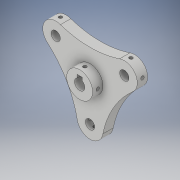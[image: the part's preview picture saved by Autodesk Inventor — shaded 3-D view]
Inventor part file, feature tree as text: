
AUTODESK INVENTOR PART (.ipt)
format: ipt  version: 2019 (Build 230136000, 136)  size: 257,536 bytes
history: native  units: mm
features: plane x10, sketch x9, hole x6, extrude x4, mirror x2, projected_geometry x2, other x1
ambient origin geometry x8: Origin, YZ Plane, XZ Plane, XY Plane, X Axis, Y Axis, Z Axis, Center Point
bodies: Body1 (feature_tree)
feature tree (34):
  other  "實體1"
  extrude  "擠出1"  Depth=109.5mm
  extrude  "擠出2"  Depth=43.5mm
  extrude  "擠出3"  Depth=76.5mm
  extrude  "擠出4"  Depth=25.0mm
  plane  "工作平面1"
  plane  "工作平面2"
  sketch  "草圖5"
  sketch  "草圖6"
  hole  "孔1"  [1 undecoded]
  hole  "孔2"  [1 undecoded]
  plane  "工作平面4"
  plane  "工作平面9"
  plane  "工作平面11"
  plane  "工作平面12"
  sketch  "草圖10"
  sketch  "草圖11"
  hole  "孔3"  [1 undecoded]
  hole  "孔4"  [1 undecoded]
  mirror  "鏡射1"
  hole  "孔5"  [1 undecoded]
  mirror  "鏡射2"
  plane  "工作平面14"
  plane  "工作平面15"
  hole  "孔7"  [1 undecoded]
  sketch  "草圖1"
  projected_geometry  "投影迴路1"
  sketch  "草圖3"
  sketch  "草圖4"
  projected_geometry  "投影迴路2"
  plane  "工作平面10"
  sketch  "草圖14"
  plane  "工作平面13"
  sketch  "草圖16"
note: 6 required parameter values undecoded (feature->parameter linkage not recoverable at this tier; creation-order binding heuristic only, values carry confidence <= 0.55)
